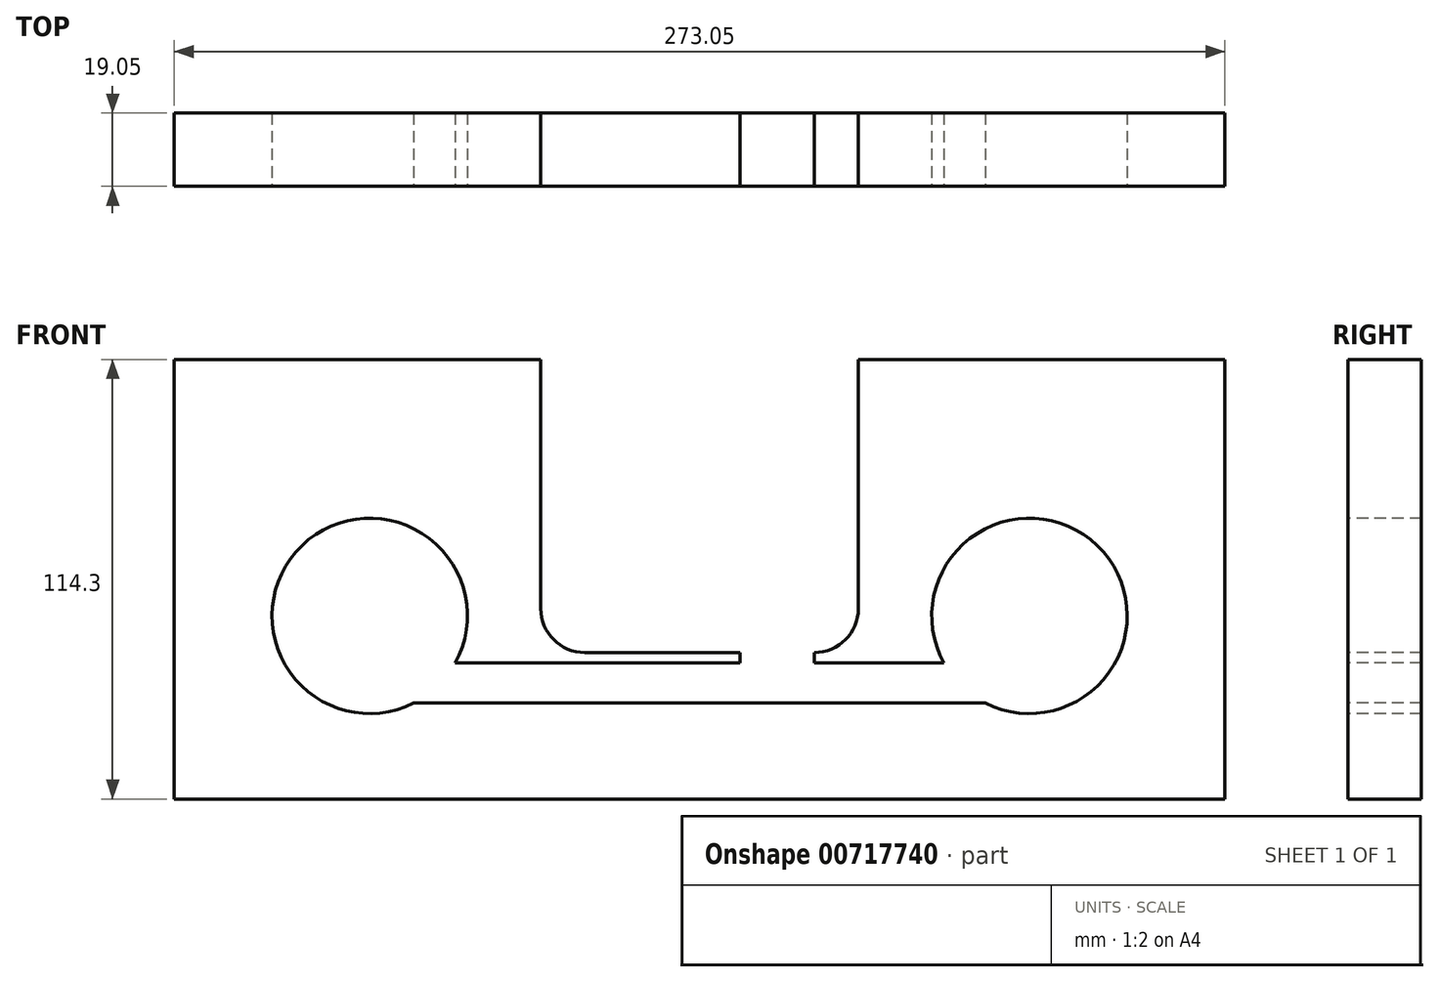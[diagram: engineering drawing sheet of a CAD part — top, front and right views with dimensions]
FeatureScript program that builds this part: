
annotation { "Feature Type Name" : "Feature", "Feature Type Description" : "" }
export const myFeature = defineFeature(function(context is Context, id is Id, definition is map)
    precondition{}
    {
        {
            var Q0;
            Q0=qCreatedBy(makeId("Front.planeOp"),FACE);
            var sketch = newSketch(context, id + "F0", { "sketchPlane" : qUnion([Q0])});
            skLineSegment(sketch, "E0.bottom", {"start": v(0, 0) * mm, "end": v(273.05, 0) * mm});
            skLineSegment(sketch, "E0.top", {"start": v(0, 114.3) * mm, "end": v(273.05, 114.3) * mm});
            skLineSegment(sketch, "E0.left", {"start": v(0, 0) * mm, "end": v(0, 114.3) * mm});
            skLineSegment(sketch, "E0.right", {"start": v(273.05, 0) * mm, "end": v(273.05, 114.3) * mm});
            skSolve(sketch);
        }
        {
            var Q0;
            Q0=makeQuery(id+"F0.imprint","IMPRINT",FACE,{"disambiguationData":[TD([[makeQuery(id+"F0.imprint","IMPRINT",EDGE,{"derivedFrom":sQuery(id+"F0.wireOp",EDGE,"E0.bottom")}),1.0]])]});
            extrude(context, id + "F1", {"entities" : qUnion([Q0]), "depth" : 19.05 * mm, "offsetDistance" : 25.4 * mm});
        }
        {
            var Q0;
            Q0=makeQuery(id+"F1.opExtrude","CAP_FACE",FACE,{"disambiguationData":[OSD([sQuery(id+"F0.wireOp",EDGE,"E0.bottom"),sQuery(id+"F0.wireOp",EDGE,"E0.top"),sQuery(id+"F0.wireOp",EDGE,"E0.left"),sQuery(id+"F0.wireOp",EDGE,"E0.right")])],"isStart":false});
            var sketch = newSketch(context, id + "F2", { "sketchPlane" : qUnion([Q0])});
            skCircle(sketch, "E1", {"center": v(50.8, 47.63) * mm, "radius": 25.4 * mm});
            skCircle(sketch, "E2", {"center": v(222.25, 47.63) * mm, "radius": 25.4 * mm});
            skSolve(sketch);
        }
        {
            var Q0;
            Q0=qSketchRegion(id+"F3U8X73pEVCCaN3_1",true);
            var Q1;
            Q1=makeQuery(id+"F2.imprint","IMPRINT",FACE,{"disambiguationData":[TD([[makeQuery(id+"F2.imprint","IMPRINT",EDGE,{"derivedFrom":sQuery(id+"F2.wireOp",EDGE,"E1")}),1.0]])]});
            var Q2;
            Q2=makeQuery(id+"F2.imprint","IMPRINT",FACE,{"disambiguationData":[TD([[makeQuery(id+"F2.imprint","IMPRINT",EDGE,{"derivedFrom":sQuery(id+"F2.wireOp",EDGE,"E2")}),1.0]])]});
            extrude(context, id + "F3", {"entities" : qUnion([Q0, Q1, Q2]), "operationType" : NewBodyOperationType.REMOVE, "oppositeDirection" : true, "depth" : 25.4 * mm, "offsetDistance" : 25.4 * mm});
        }
        {
            var Q0;
            Q0=makeQuery(id+"F1.opExtrude","CAP_FACE",FACE,{"disambiguationData":[OSD([sQuery(id+"F0.wireOp",EDGE,"E0.bottom"),sQuery(id+"F0.wireOp",EDGE,"E0.top"),sQuery(id+"F0.wireOp",EDGE,"E0.left"),sQuery(id+"F0.wireOp",EDGE,"E0.right")])],"isStart":false});
            var sketch = newSketch(context, id + "F4", { "sketchPlane" : qUnion([Q0])});
            skLineSegment(sketch, "E3", {"start": v(73.03, 35.34) * mm, "end": v(200.02, 35.34) * mm});
            skLineSegment(sketch, "E4", {"start": v(62.23, 24.94) * mm, "end": v(210.82, 24.94) * mm});
            skSolve(sketch);
        }
        {
            var Q0;
            {var subQ0=sQuery(id+"F4.wireOp",EDGE,"E3");Q0=makeQuery(id+"F4.imprint","IMPRINT",FACE,{"disambiguationData":[TD([[makeQuery(id+"F4.imprint","IMPRINT",EDGE,{"derivedFrom":subQ0}),-1.0]])]});}
            extrude(context, id + "F5", {"entities" : qUnion([Q0]), "operationType" : NewBodyOperationType.REMOVE, "oppositeDirection" : true, "depth" : 25.4 * mm, "offsetDistance" : 25.4 * mm});
        }
        {
            var Q0;
            Q0=makeQuery(id+"F1.opExtrude","CAP_FACE",FACE,{"disambiguationData":[OSD([sQuery(id+"F0.wireOp",EDGE,"E0.bottom"),sQuery(id+"F0.wireOp",EDGE,"E0.top"),sQuery(id+"F0.wireOp",EDGE,"E0.left"),sQuery(id+"F0.wireOp",EDGE,"E0.right")])],"isStart":false});
            var sketch = newSketch(context, id + "F6", { "sketchPlane" : qUnion([Q0])});
            skLineSegment(sketch, "E5", {"start": v(95.25, 114.3) * mm, "end": v(95.25, 49.53) * mm});
            skLineSegment(sketch, "E6", {"start": v(106.68, 38.1) * mm, "end": v(166.37, 38.1) * mm});
            skLineSegment(sketch, "E7", {"start": v(177.8, 49.53) * mm, "end": v(177.8, 114.3) * mm});
            skPoint(sketch, "E8.visualSharp", {"position": v(95.25, 38.1) * mm});
            skArc(sketch, "E8.filletArc", {"start": v(95.25, 49.53) * mm, "mid": v(98.6, 41.45) * mm, "end": v(106.68, 38.1) * mm});
            skPoint(sketch, "E9.visualSharp", {"position": v(177.8, 38.1) * mm});
            skArc(sketch, "E9.filletArc", {"start": v(166.37, 38.1) * mm, "mid": v(174.45, 41.45) * mm, "end": v(177.8, 49.53) * mm});
            skSolve(sketch);
        }
        {
            var Q0;
            Q0 = qSketchRegion(id + "F6", true);
            var Q1;
            {var subQ0=sQuery(id+"F6.wireOp",EDGE,"E5");Q1=makeQuery(id+"F6.imprint","IMPRINT",FACE,{"disambiguationData":[TD([[makeQuery(id+"F6.imprint","IMPRINT",EDGE,{"derivedFrom":subQ0}),1.0]])]});}
            extrude(context, id + "F7", {"entities" : qUnion([Q0, Q1]), "operationType" : NewBodyOperationType.REMOVE, "oppositeDirection" : true, "depth" : 25.4 * mm, "offsetDistance" : 25.4 * mm});
        }
        {
            var Q0;
            Q0=makeQuery(id+"F1.opExtrude","CAP_FACE",FACE,{"disambiguationData":[OSD([sQuery(id+"F0.wireOp",EDGE,"E0.bottom"),sQuery(id+"F0.wireOp",EDGE,"E0.top"),sQuery(id+"F0.wireOp",EDGE,"E0.left"),sQuery(id+"F0.wireOp",EDGE,"E0.right")])],"isStart":false});
            var sketch = newSketch(context, id + "F8", { "sketchPlane" : qUnion([Q0])});
            skLineSegment(sketch, "E10", {"start": v(147.03, 38.1) * mm, "end": v(147.03, 35.34) * mm});
            skLineSegment(sketch, "E11", {"start": v(166.37, 38.1) * mm, "end": v(166.37, 35.34) * mm});
            skSolve(sketch);
        }
        {
            var Q0;
            Q0 = qSketchRegion(id + "F8", true);
            var Q1;
            {var subQ0=sQuery(id+"F8.wireOp",EDGE,"E10");Q1=makeQuery(id+"F8.imprint","IMPRINT",FACE,{"disambiguationData":[TD([[makeQuery(id+"F8.imprint","IMPRINT",EDGE,{"derivedFrom":subQ0}),1.0]])]});}
            extrude(context, id + "F9", {"entities" : qUnion([Q0, Q1]), "operationType" : NewBodyOperationType.REMOVE, "oppositeDirection" : true, "depth" : 25.4 * mm, "offsetDistance" : 25.4 * mm});
        }
    });
